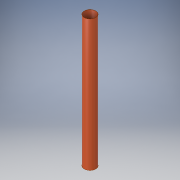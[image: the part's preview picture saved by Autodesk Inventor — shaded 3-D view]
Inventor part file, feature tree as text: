
AUTODESK INVENTOR PART (.ipt)
format: ipt  version: 2017 (Build 210142000, 142)  size: 94,720 bytes
history: native  units: in
note: dims shown in document units (in); Inventor stores cm internally (conversion verified against a paired STEP export)
features: extrude x1, sketch x1
ambient origin geometry x8: Origin, YZ Plane, XZ Plane, XY Plane, X Axis, Y Axis, Z Axis, Center Point
bodies: Solid1 (feature_tree)
feature tree (2):
  extrude  "Extrusion1"  Depth=84.0in TaperAngle=0.0deg
  sketch  "Sketch1"  dims[d1=7.25in d2=84.0in d3=0.0in d4=7.4in]
